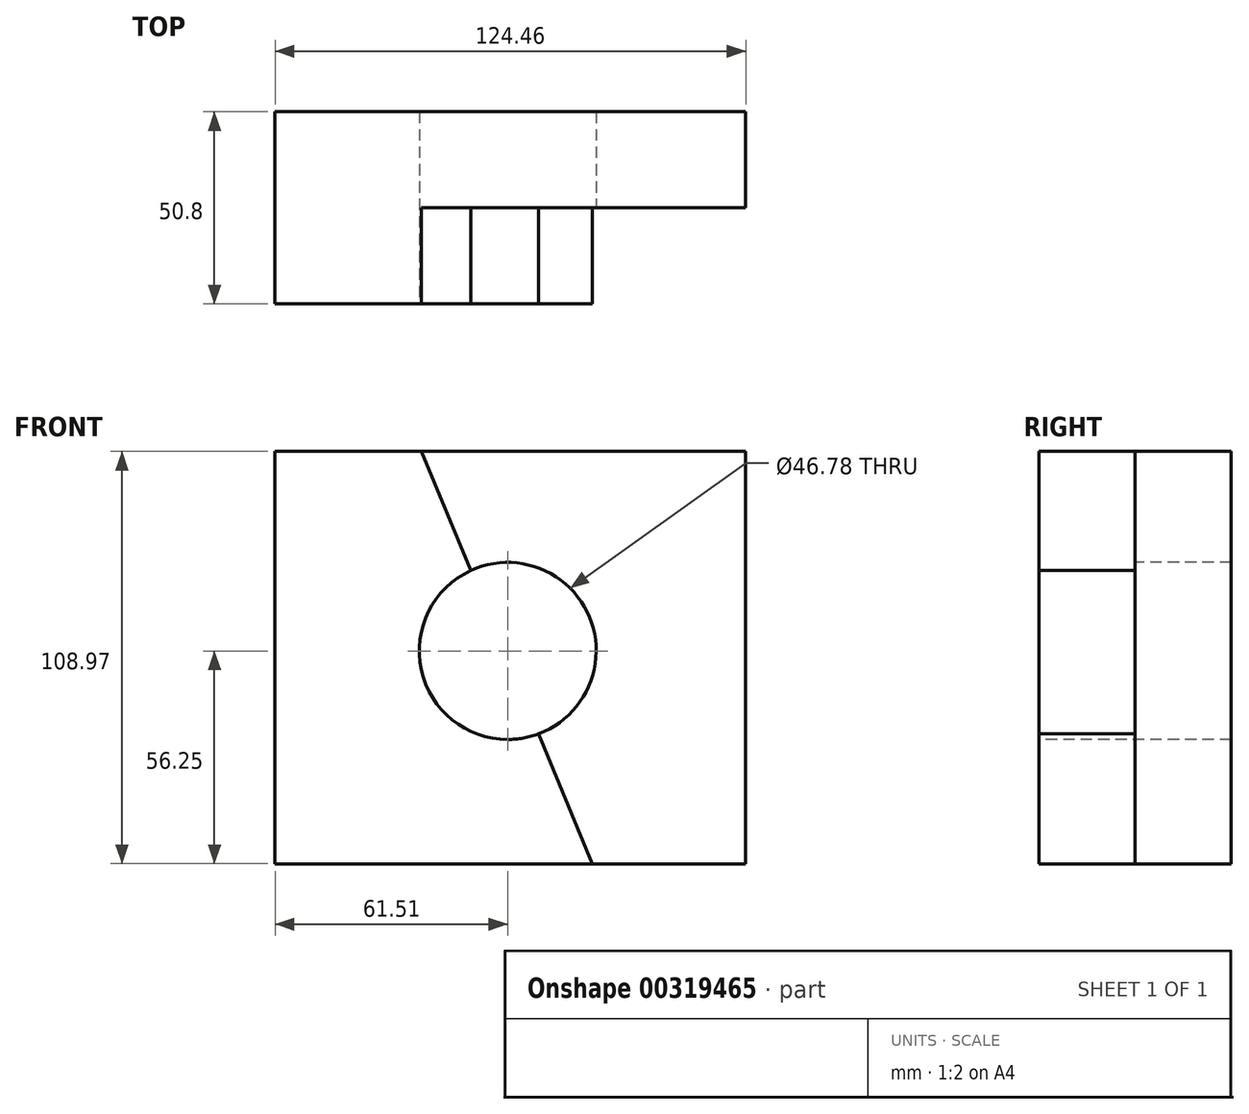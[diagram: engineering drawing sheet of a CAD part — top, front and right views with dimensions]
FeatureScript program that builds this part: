
annotation { "Feature Type Name" : "Feature", "Feature Type Description" : "" }
export const myFeature = defineFeature(function(context is Context, id is Id, definition is map)
    precondition{}
    {
        {
            var Q0;
            Q0=qCreatedBy(makeId("Front.planeOp"),FACE);
            var sketch = newSketch(context, id + "F0", { "sketchPlane" : qUnion([Q0])});
            skLineSegment(sketch, "E0.bottom", {"start": v(-61.51, 52.72) * mm, "end": v(62.95, 52.72) * mm});
            skLineSegment(sketch, "E0.top", {"start": v(-61.51, -56.25) * mm, "end": v(62.95, -56.25) * mm});
            skLineSegment(sketch, "E0.left", {"start": v(-61.51, 52.72) * mm, "end": v(-61.51, -56.25) * mm});
            skLineSegment(sketch, "E0.right", {"start": v(62.95, 52.72) * mm, "end": v(62.95, -56.25) * mm});
            skSolve(sketch);
        }
        {
            var Q0;
            Q0 = qSketchRegion(id + "F0", true);
            extrude(context, id + "F1", {"entities" : qUnion([Q0]), "depth" : 25.4 * mm, "offsetDistance" : 25.4 * mm});
        }
        {
            var Q0;
            Q0=makeQuery(id+"F1.opExtrude","CAP_FACE",FACE,{"disambiguationData":[OSD([sQuery(id+"F0.wireOp",EDGE,"E0.bottom"),sQuery(id+"F0.wireOp",EDGE,"E0.top"),sQuery(id+"F0.wireOp",EDGE,"E0.left"),sQuery(id+"F0.wireOp",EDGE,"E0.right")])],"isStart":false});
            var sketch = newSketch(context, id + "F2", { "sketchPlane" : qUnion([Q0])});
            skLineSegment(sketch, "E1", {"start": v(-22.82, 52.72) * mm, "end": v(22.38, -56.25) * mm});
            skSolve(sketch);
        }
        {
            var Q0;
            {var subQ0=sQuery(id+"F2.wireOp",EDGE,"E1");Q0=makeQuery(id+"F2.imprint","IMPRINT",FACE,{"disambiguationData":[TD([[makeQuery(id+"F2.imprint","IMPRINT",EDGE,{"derivedFrom":subQ0}),-1.0]])]});}
            extrude(context, id + "F3", {"entities" : qUnion([Q0]), "operationType" : NewBodyOperationType.ADD, "depth" : 25.4 * mm, "offsetDistance" : 25.4 * mm});
        }
        {
            var Q0;
            Q0=makeQuery(id+"F3.opExtrude","CAP_FACE",FACE,{"disambiguationData":[OSD([sQuery(id+"F0.wireOp",EDGE,"E0.bottom"),sQuery(id+"F0.wireOp",EDGE,"E0.top"),sQuery(id+"F0.wireOp",EDGE,"E0.left"),sQuery(id+"F2.wireOp",EDGE,"E1")])],"isStart":false});
            var sketch = newSketch(context, id + "F4", { "sketchPlane" : qUnion([Q0])});
            skCircle(sketch, "E2", {"center": v(0, 0) * mm, "radius": 23.4 * mm});
            skSolve(sketch);
        }
        {
            var Q0;
            {var subQ0=sQuery(id+"F4.wireOp",EDGE,"E2");var subQ1=makeQuery(id+"F3.opExtrude","CAP_EDGE",EDGE,{"disambiguationData":[OSD([sQuery(id+"F2.wireOp",EDGE,"E1")])],"isStart":false});var subQ2=makeQuery(id+"F4.imprint","INTERSECT",VERTEX,{"disambiguationData":[OD(0.0)],"derivedFrom":[subQ1,subQ0]});Q0=makeQuery(id+"F4.imprint","IMPRINT",FACE,{"disambiguationData":[TD([[makeQuery(id+"F4.imprint","IMPRINT",EDGE,{"disambiguationData":[TD([[subQ2,-1.0]])],"derivedFrom":subQ0}),1.0]])]});}
            var Q1;
            {var subQ0=sQuery(id+"F4.wireOp",EDGE,"E2");var subQ1=makeQuery(id+"F3.opExtrude","CAP_EDGE",EDGE,{"disambiguationData":[OSD([sQuery(id+"F2.wireOp",EDGE,"E1")])],"isStart":false});var subQ2=makeQuery(id+"F4.imprint","INTERSECT",VERTEX,{"disambiguationData":[OD(0.0)],"derivedFrom":[subQ1,subQ0]});Q1=makeQuery(id+"F4.imprint","IMPRINT",FACE,{"disambiguationData":[TD([[makeQuery(id+"F4.imprint","IMPRINT",EDGE,{"disambiguationData":[TD([[subQ2,1.0]])],"derivedFrom":subQ0}),1.0]])]});}
            extrude(context, id + "F5", {"entities" : qUnion([Q0, Q1]), "operationType" : NewBodyOperationType.REMOVE, "endBound" : BoundingType.THROUGH_ALL, "oppositeDirection" : true, "depth" : 25.4 * mm, "offsetDistance" : 25.4 * mm});
        }
    });
